# Revit family: Gira_110427
name_source: partatom
category: Electrical Fixtures
revit_build: Autodesk Revit 2017 (Build: 20160225_1515(x64)
units: mm (PartAtom-declared; Revit-internal decimal feet)

## family parameters
Cut with Voids When Loaded = No
Host = Face
Maintain Annotation Orientation = Yes
Part Type = Normal
Room Calculation Point = No
Round Connector Dimension = Use Diameter
Shared = No

## types (1)
- Rocker sw. hotel room status displ. System 55 p.white m
    Assembly arrangement = Basic element with central cover plate
    Available = No
    BIM (1) = https://media.stage.bim.site und Tasten.rfa?public/gira/36a6b08/Sys55_Komplettgerät_Schalten und Tasten.rfa
    Category = Switch
    Colour = White
    Connection type = Plug clamp
    Data sheet (1) = https://katalog.gira.de
    Default Elevation = 1219 mm
    Description = Rock.sw.h-room stat.displ. Sys55 PWm,Rocker switch, 10 AX 250 V~ with rocker, 2-gang for displaying hotel room status,,pure white matt,Features:,- Switch for hotel room status display Do not disturb" and "Make up room".,- With block to prevent both sides from being switched on.,- Locked both electrically and mechanically."
    GTIN = 4010337104278
    HAN = 110427
    Halogen free = Yes
    HeinzeBIM = https://bimportal.heinze.de
    Illumination = No
    Label space/information surface = No
    Manufacturer = Gira
    Manufacturer URL = https://www.gira.de
    Material = Plastic
    Material quality = Thermoplastic
    Method of operation = Rocker/button
    Model = Sys55_Komplettgerät_Schalten und Tasten
    Mounting method = Flush mounted (plaster)
    Name = Rocker sw. hotel room status displ. System 55 p.white m
    Nominal voltage = 250
    Number of modules (module system) = 1
    Number of rockers = 2
    Push button switch = No
    RAL-number (akin) = 9010
    Rated current = 10
    Suitable for degree of protection (IP) = IP20
    Surface finishing = Matt
    Surface protection = Other
    Type of fastening = Mounting with claw and screw
    URL = http://katalog.gira.de
    Washing machine switch = No
    Wiring system = Series switch
    With mounting plate = No

## geometry (parser evidence)
native form markers: Sweep x8
no freeform markers — native parametric forms only
